# Revit family: Shower-Handshower_Kit-KOHLER-KUMIN-K-99460T_1
name_source: partatom
category: Plumbing Fixtures
revit_build: Autodesk Revit 2017 (Build: 20160225_1515(x64)
units: mm (PartAtom-declared; Revit-internal decimal feet)

## family parameters
Cut with Voids When Loaded = No
Host = Face
OmniClass Number = 23.31.17.00
OmniClass Title = Showers
Part Type = Normal
Room Calculation Point = No
Round Connector Dimension = Use Diameter
Shared = No

## types (2) — shared parameters
ADA Compliant = No
Assembly Code = D2010700
CW Connection = Yes
Cold Water Inlet = Cold Water Inlet
Date Modified = 10/14/2020
Default Elevation = 36"
Description = Wall-mounted bathtub shower faucet
Drain Included = No
Finish = Kohler-Metal-CP-Polished_Chrome
Flow Rate = 2 GPM
HW Connection = Yes
Handle Clearance = 3 1/8"
Height = 22"
Hot Water Inlet = Hot Water Inlet
Length = 7 3/8"
Manufacturer = KOHLER Co.
Master Format 2014 = 22 42 23
Master Format 2014 Name = Residential Showers
Material = Premium Metal Construction
Pressure = 80.00 psi
Product Name = KUMIN
Spout Reach = 4 1/4"
URL = http://www.kohler.com.cn
Vent Connection = No
Waste Connection = No
Waste Water Outlet = Waste Water Outlet
WaterSense Certified = No
Width = 8 1/2"

## per-type parameters (varying)
| type | Model | Product Documentation Link | Product Page URL | Type |
| CP- Polished Chrome | K-99460T-4-CP | https://files.kohler.com.cn | https://www.kohler.com.cn | 1 |
| 4E2,CP- Polished Chrome | K-99460T-4E2-CP |  |  | 2 |

## geometry (parser evidence)
native form markers: Sweep x4
no freeform markers — native parametric forms only
